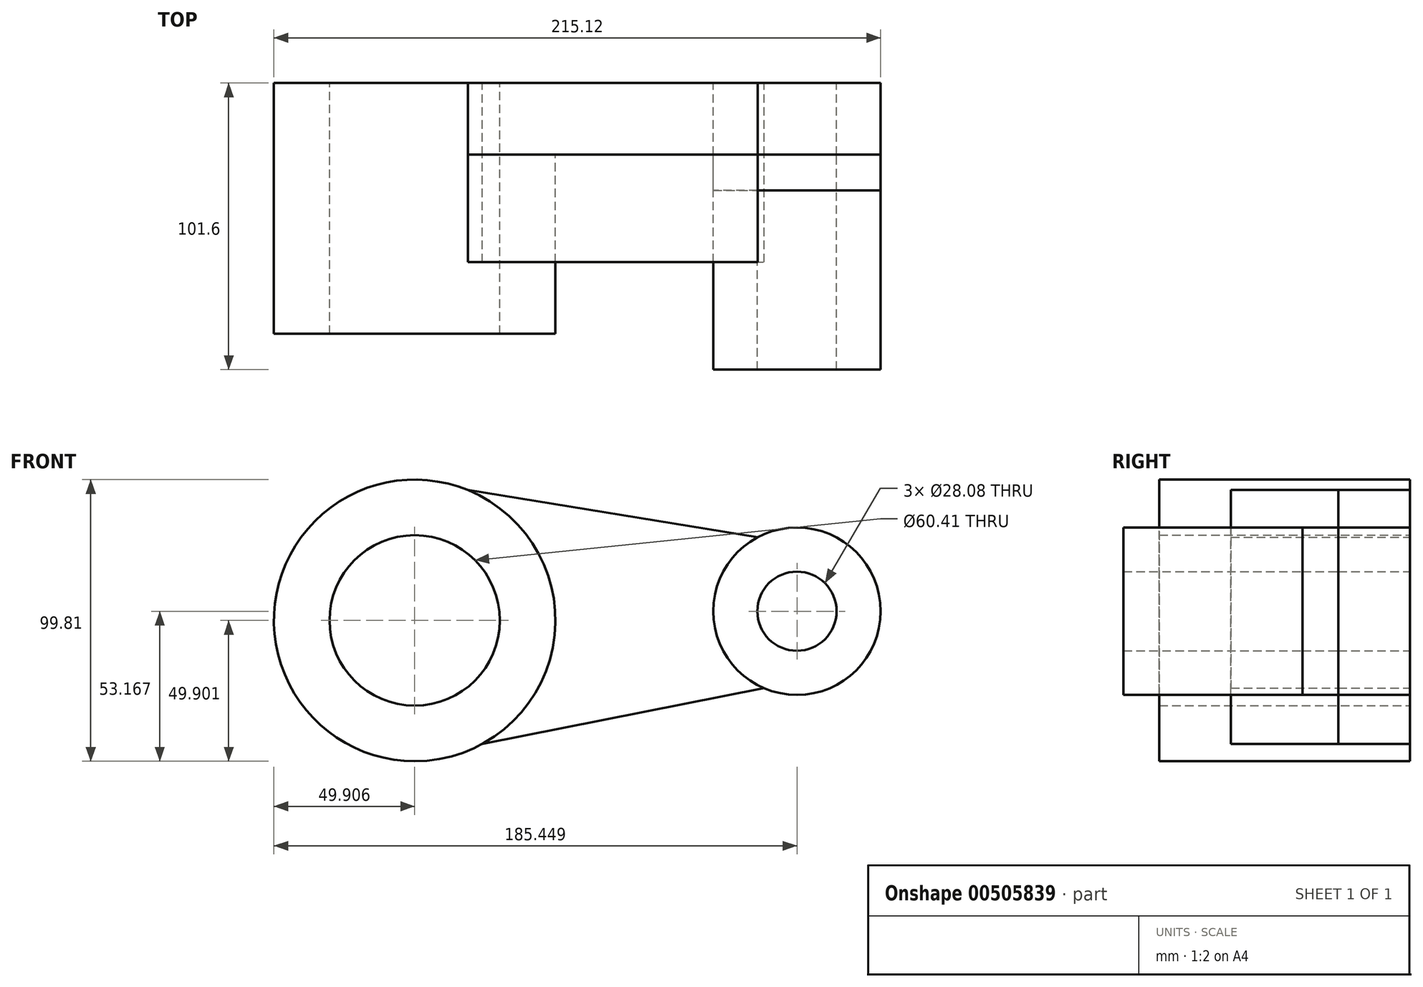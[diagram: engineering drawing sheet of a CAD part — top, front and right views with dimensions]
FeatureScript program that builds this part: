
annotation { "Feature Type Name" : "Feature", "Feature Type Description" : "" }
export const myFeature = defineFeature(function(context is Context, id is Id, definition is map)
    precondition{}
    {
        {
            var Q0;
            Q0=qCreatedBy(makeId("Front.planeOp"),FACE);
            var sketch = newSketch(context, id + "F0", { "sketchPlane" : qUnion([Q0])});
            skCircle(sketch, "E0", {"center": v(-69.93, 27.9) * mm, "radius": 49.9 * mm});
            skCircle(sketch, "E1", {"center": v(65.6, 31.16) * mm, "radius": 29.67 * mm});
            skLineSegment(sketch, "E2", {"start": v(-51.07, 74.1) * mm, "end": v(51.63, 57.33) * mm});
            skLineSegment(sketch, "E3", {"start": v(-45.93, -15.86) * mm, "end": v(53.93, 3.88) * mm});
            skCircle(sketch, "E4", {"center": v(-69.93, 27.9) * mm, "radius": 30.2 * mm});
            skCircle(sketch, "E5", {"center": v(65.6, 31.16) * mm, "radius": 14.04 * mm});
            skSolve(sketch);
        }
        {
            var Q0;
            {var subQ0=sQuery(id+"F0.wireOp",EDGE,"E2");Q0=makeQuery(id+"F0.imprint","IMPRINT",FACE,{"disambiguationData":[TD([[makeQuery(id+"F0.imprint","IMPRINT",EDGE,{"derivedFrom":subQ0}),-1.0]])]});}
            var sketch = newSketch(context, id + "F1", { "sketchPlane" : qUnion([Q0])});
            skSolve(sketch);
        }
        {
            var Q0;
            Q0=makeQuery(id+"F0.imprint","IMPRINT",FACE,{"disambiguationData":[TD([[makeQuery(id+"F0.imprint","IMPRINT",EDGE,{"derivedFrom":sQuery(id+"F0.wireOp",EDGE,"E5")}),-1.0]])]});
            var Q1;
            Q1=makeQuery(id+"F0.imprint","IMPRINT",FACE,{"disambiguationData":[TD([[makeQuery(id+"F0.imprint","IMPRINT",EDGE,{"derivedFrom":sQuery(id+"F0.wireOp",EDGE,"E4")}),-1.0]])]});
            var Q2;
            {var subQ0=sQuery(id+"F0.wireOp",EDGE,"E2");Q2=makeQuery(id+"F1.imprint","IMPRINT",FACE,{"disambiguationData":[TD([[makeQuery(id+"F1.imprint","IMPRINT",EDGE,{"derivedFrom":makeQuery(id+"F0.imprint","IMPRINT",EDGE,{"derivedFrom":subQ0})}),-1.0]])]});}
            extrude(context, id + "F2", {"entities" : qUnion([Q0, Q1, Q2]), "depth" : 25.4 * mm, "offsetDistance" : 25.4 * mm});
        }
        {
            var Q0;
            Q0=qCreatedBy(makeId("Front.planeOp"),FACE);
            var sketch = newSketch(context, id + "F3", { "sketchPlane" : qUnion([Q0])});
            skSolve(sketch);
        }
        {
            var Q0;
            Q0 = qSketchRegion(id + "F3", true);
            var Q1;
            Q1=makeQuery(id+"F2.opExtrude","CAP_FACE",FACE,{"disambiguationData":[OSD([sQuery(id+"F0.wireOp",EDGE,"E0"),sQuery(id+"F0.wireOp",EDGE,"E4")])],"isStart":false});
            extrude(context, id + "F4", {"entities" : qUnion([Q0, Q1]), "operationType" : NewBodyOperationType.ADD, "depth" : 63.5 * mm, "offsetDistance" : 25.4 * mm});
        }
        {
            var Q0;
            Q0=makeQuery(id+"F2.opExtrude","CAP_FACE",FACE,{"disambiguationData":[OSD([sQuery(id+"F0.wireOp",EDGE,"E0"),sQuery(id+"F0.wireOp",EDGE,"E1"),sQuery(id+"F0.wireOp",EDGE,"E2"),sQuery(id+"F0.wireOp",EDGE,"E3")])],"isStart":false});
            extrude(context, id + "F5", {"entities" : qUnion([Q0]), "depth" : 38.1 * mm, "offsetDistance" : 25.4 * mm});
        }
        {
            var Q0;
            Q0=makeQuery(id+"F2.opExtrude","CAP_FACE",FACE,{"disambiguationData":[OSD([sQuery(id+"F0.wireOp",EDGE,"E1"),sQuery(id+"F0.wireOp",EDGE,"E5")])],"isStart":false});
            extrude(context, id + "F6", {"entities" : qUnion([Q0]), "depth" : 12.7 * mm, "offsetDistance" : 25.4 * mm});
        }
        {
            var Q0;
            Q0=makeQuery(id+"F6.opExtrude","CAP_FACE",FACE,{"disambiguationData":[OSD([sQuery(id+"F0.wireOp",EDGE,"E1"),sQuery(id+"F0.wireOp",EDGE,"E5")])],"isStart":false});
            extrude(context, id + "F7", {"entities" : qUnion([Q0]), "depth" : 63.5 * mm, "offsetDistance" : 25.4 * mm});
        }
    });
